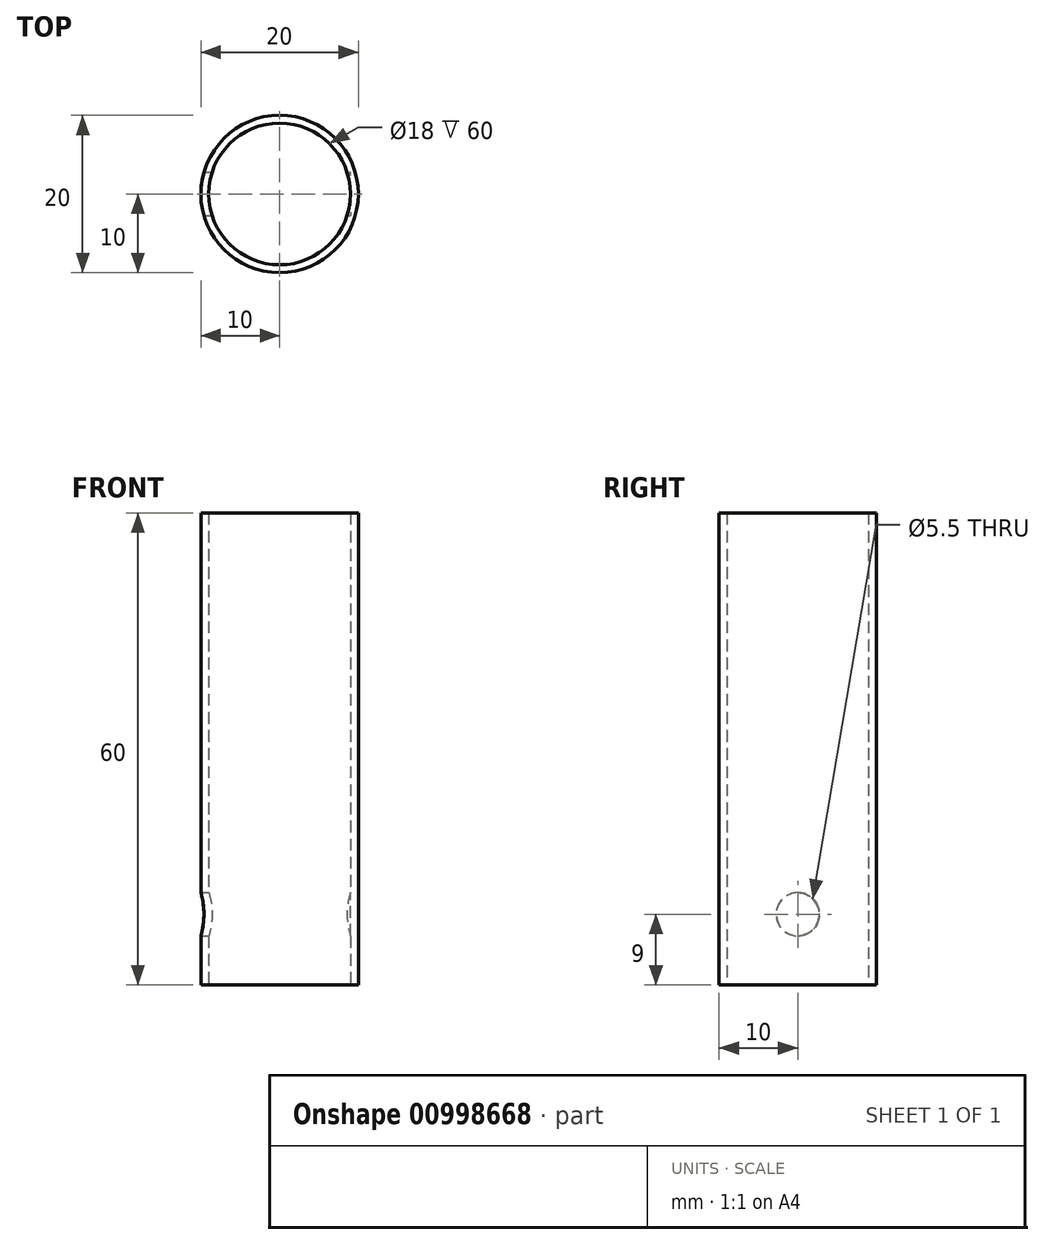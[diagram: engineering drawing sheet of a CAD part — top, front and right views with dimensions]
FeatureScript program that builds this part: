
annotation { "Feature Type Name" : "Feature", "Feature Type Description" : "" }
export const myFeature = defineFeature(function(context is Context, id is Id, definition is map)
    precondition{}
    {
        {
            var Q0;
            Q0=qCreatedBy(makeId("Top.planeOp"),FACE);
            var sketch = newSketch(context, id + "F0", { "sketchPlane" : qUnion([Q0])});
            skCircle(sketch, "E0", {"center": v(0, 0) * mm, "radius": 10 * mm});
            skCircle(sketch, "E1.0", {"center": v(0, 0) * mm, "radius": 9 * mm});
            skSolve(sketch);
        }
        {
            var Q0;
            Q0=makeQuery(id+"F0.imprint","IMPRINT",FACE,{"disambiguationData":[TD([[makeQuery(id+"F0.imprint","IMPRINT",EDGE,{"derivedFrom":sQuery(id+"F0.wireOp",EDGE,"E0")}),1.0]])]});
            extrude(context, id + "F1", {"entities" : qUnion([Q0]), "endBound" : BoundingType.SYMMETRIC, "depth" : 60 * mm, "offsetDistance" : 25 * mm});
        }
        {
            var Q0;
            Q0=qCreatedBy(makeId("Right.planeOp"),FACE);
            var sketch = newSketch(context, id + "F2", { "sketchPlane" : qUnion([Q0])});
            skCircle(sketch, "E2", {"center": v(0, -21) * mm, "radius": 2.75 * mm});
            skSolve(sketch);
        }
        {
            var Q0;
            Q0=qSketchRegion(id+"F2",true);
            extrude(context, id + "F3", {"entities" : qUnion([Q0]), "operationType" : NewBodyOperationType.REMOVE, "oppositeDirection" : true, "depth" : 25 * mm, "offsetDistance" : 25 * mm, "hasSecondDirection" : true, "secondDirectionOppositeDirection" : false, "secondDirectionDepth" : 9 * mm});
        }
    });
